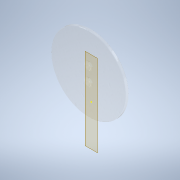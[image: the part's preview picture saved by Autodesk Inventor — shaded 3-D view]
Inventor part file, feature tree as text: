
AUTODESK INVENTOR PART (.ipt)
format: ipt  version: 2021 (Build 250183000, 183)  size: 138,752 bytes
history: native  units: mm
features: other x6, sketch x3, chamfer x2, reference x2, extrude x1
ambient origin geometry x8: Origin, YZ Plane, XZ Plane, XY Plane, X Axis, Y Axis, Z Axis, Center Point
bodies: Body1 (feature_tree)
feature tree (14):
  other  "Bryła1"
  other  "Płaszczyzna konstrukcyjna1"
  extrude  "Wyciągnięcie proste1"  Depth=7.5mm
  chamfer  "Faza1"  Distance=7.5mm
  chamfer  "Faza3"  Distance=80.0mm
  sketch  "Szkic2"
  sketch  "Szkic3"
  sketch  "Szkic1"
  reference  "Odniesienie1"
  reference  "Odniesienie2"
  parser-record x1  (decoder bookkeeping rows leaked as tree rows — omitted from the tree; the rows remain in map.json)
  other  "model tensometru.iam"
  other  "tensometr:1"
  other  "Zespół1"
note: 1 file-system path scrubbed to <path> (originals preserved in map.json)
